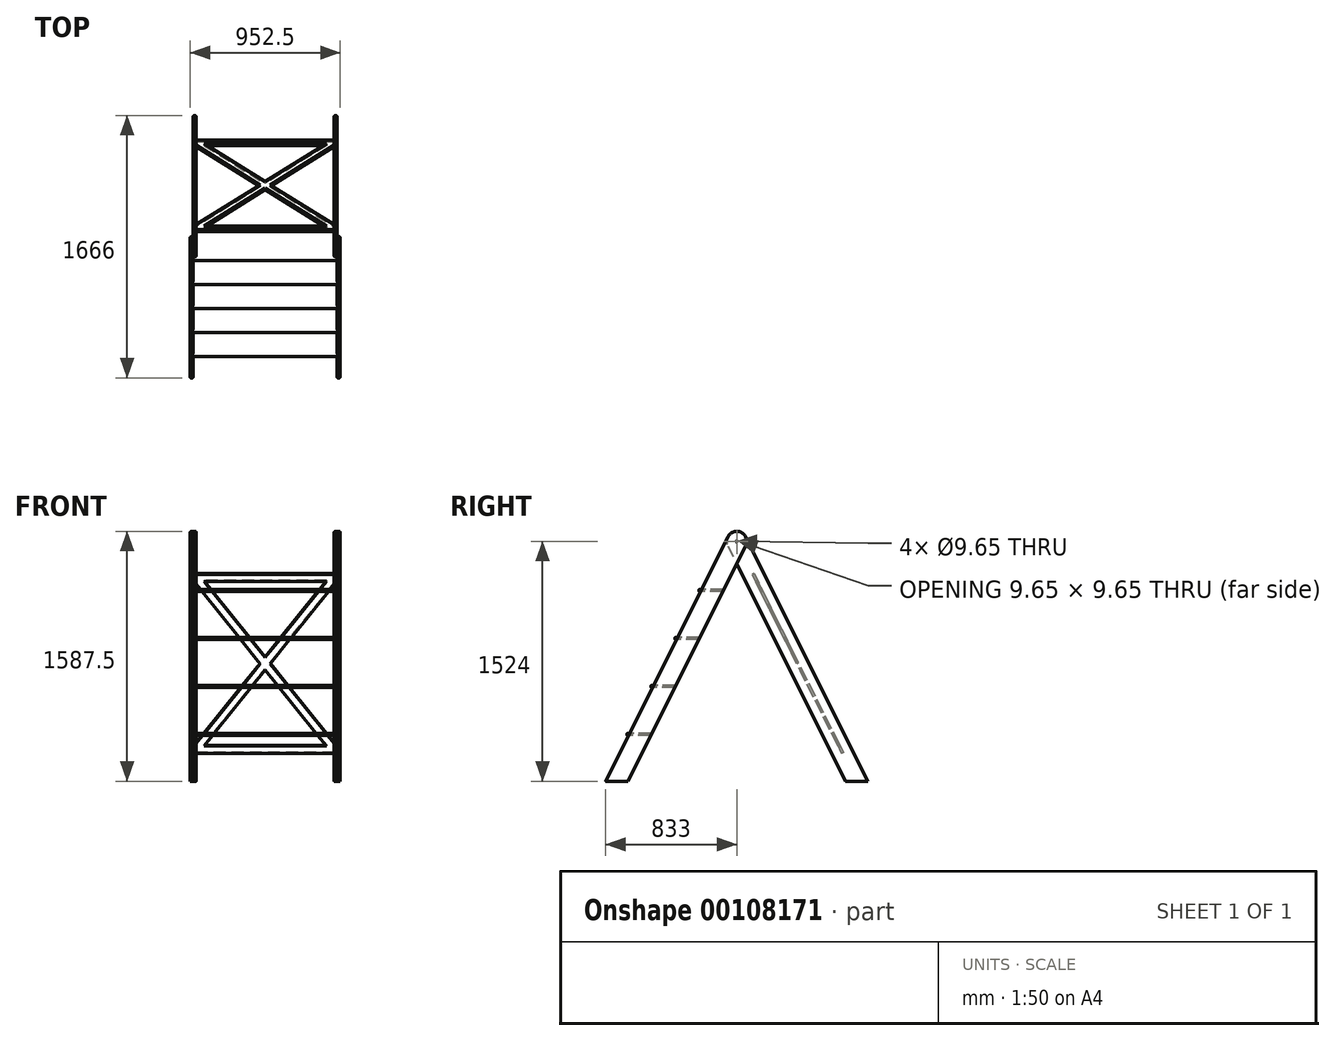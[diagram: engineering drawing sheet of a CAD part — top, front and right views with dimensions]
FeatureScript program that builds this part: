
annotation { "Feature Type Name" : "Feature", "Feature Type Description" : "" }
export const myFeature = defineFeature(function(context is Context, id is Id, definition is map)
    precondition{}
    {
        {
            var Q0;
            Q0=qCreatedBy(makeId("Right.planeOp"),FACE);
            var sketch = newSketch(context, id + "F0", { "sketchPlane" : qUnion([Q0])});
            skLineSegment(sketch, "E0", {"start": v(0, 0) * mm, "end": v(0, 1524) * mm, "construction": true});
            skLineSegment(sketch, "E1.0", {"start": v(-762, 0) * mm, "end": v(-762, 1524) * mm, "construction": true});
            skLineSegment(sketch, "E2", {"start": v(-691, 0) * mm, "end": v(-833, 0) * mm});
            skLineSegment(sketch, "E3.0", {"start": v(0, 304.8) * mm, "end": v(-1233.58, 304.8) * mm, "construction": true});
            skLineSegment(sketch, "E4.0", {"start": v(0, 609.6) * mm, "end": v(-1233.58, 609.6) * mm, "construction": true});
            skLineSegment(sketch, "E5.0", {"start": v(0, 914.4) * mm, "end": v(-1233.58, 914.4) * mm, "construction": true});
            skLineSegment(sketch, "E6.0", {"start": v(0, 1219.2) * mm, "end": v(-1233.58, 1219.2) * mm, "construction": true});
            skArc(sketch, "E7", {"start": v(-28.4, 1467.2) * mm, "mid": v(-14.59, 1462.2) * mm, "end": v(0, 1460.5) * mm, "construction": true});
            skLineSegment(sketch, "E8", {"start": v(0, 1524) * mm, "end": v(-762, 0) * mm, "construction": true});
            skLineSegment(sketch, "E9.0", {"start": v(-56.8, 1552.4) * mm, "end": v(-833, 0) * mm});
            skLineSegment(sketch, "E10.0", {"start": v(56.8, 1495.6) * mm, "end": v(-691, 0) * mm});
            skArc(sketch, "E11.trimOffspring", {"start": v(56.8, 1495.6) * mm, "mid": v(28.4, 1580.8) * mm, "end": v(-56.8, 1552.4) * mm});
            skSolve(sketch);
        }
        {
            var Q0;
            Q0 = qSketchRegion(id + "F0", true);
            extrude(context, id + "F1", {"entities" : qUnion([Q0]), "depth" : 19.05 * mm});
        }
        {
            var Q0;
            Q0=makeQuery(id+"F1.opExtrude","CAP_FACE",FACE,{"disambiguationData":[OSD([sQuery(id+"F0.wireOp",EDGE,"E2"),sQuery(id+"F0.wireOp",EDGE,"E9.0"),sQuery(id+"F0.wireOp",EDGE,"E10.0"),sQuery(id+"F0.wireOp",EDGE,"E11.trimOffspring")])],"isStart":true});
            var sketch = newSketch(context, id + "F2", { "sketchPlane" : qUnion([Q0])});
            skLineSegment(sketch, "E12.0", {"start": v(56.8, 1552.4) * mm, "end": v(229.75, 1206.5) * mm});
            skLineSegment(sketch, "E13.0", {"start": v(-56.8, 1495.6) * mm, "end": v(87.75, 1206.5) * mm});
            skLineSegment(sketch, "E14.0", {"start": v(0, 1219.2) * mm, "end": v(1233.58, 1219.2) * mm});
            skLineSegment(sketch, "E15.0", {"start": v(0, 914.4) * mm, "end": v(1233.58, 914.4) * mm});
            skLineSegment(sketch, "E16.0", {"start": v(0, 609.6) * mm, "end": v(1233.58, 609.6) * mm});
            skLineSegment(sketch, "E17.0", {"start": v(0, 304.8) * mm, "end": v(1233.58, 304.8) * mm});
            skLineSegment(sketch, "E18.0", {"start": v(0, 1206.5) * mm, "end": v(1233.58, 1206.5) * mm});
            skLineSegment(sketch, "E19.0", {"start": v(0, 901.7) * mm, "end": v(1233.58, 901.7) * mm});
            skLineSegment(sketch, "E20.0", {"start": v(0, 596.9) * mm, "end": v(1233.58, 596.9) * mm});
            skLineSegment(sketch, "E21.0", {"start": v(0, 292.1) * mm, "end": v(1233.58, 292.1) * mm});
            skLineSegment(sketch, "E22.trimOffspring", {"start": v(375.8, 914.4) * mm, "end": v(382.15, 901.7) * mm});
            skLineSegment(sketch, "E23.trimOffspring", {"start": v(233.8, 914.4) * mm, "end": v(240.15, 901.7) * mm});
            skLineSegment(sketch, "E24.trimOffspring", {"start": v(528.2, 609.6) * mm, "end": v(534.55, 596.9) * mm});
            skLineSegment(sketch, "E25.trimOffspring", {"start": v(386.2, 609.6) * mm, "end": v(392.55, 596.9) * mm});
            skLineSegment(sketch, "E26.trimOffspring", {"start": v(680.6, 304.8) * mm, "end": v(686.95, 292.1) * mm});
            skLineSegment(sketch, "E27.trimOffspring", {"start": v(538.6, 304.8) * mm, "end": v(544.95, 292.1) * mm});
            skPoint(sketch, "E28.orphan", {"position": v(833, 0) * mm});
            skPoint(sketch, "E29.orphan", {"position": v(691, 0) * mm});
            skSolve(sketch);
        }
        {
            var Q0;
            Q0 = qSketchRegion(id + "F2", true);
            extrude(context, id + "F3", {"entities" : qUnion([Q0]), "operationType" : NewBodyOperationType.REMOVE, "oppositeDirection" : true, "depth" : 6.35 * mm});
        }
        {
            var Q0;
            Q0=makeQuery(id+"F0.imprint","IMPRINT",FACE,{"disambiguationData":[TD([[makeQuery(id+"F0.imprint","IMPRINT",EDGE,{"derivedFrom":sQuery(id+"F0.wireOp",EDGE,"E2")}),-1.0]])]});
            var sketch = newSketch(context, id + "F4", { "sketchPlane" : qUnion([Q0])});
            skLineSegment(sketch, "E30.0", {"start": v(0, 1524) * mm, "end": v(-762, 0) * mm, "construction": true});
            skPoint(sketch, "E31", {"position": v(0, 1524) * mm});
            skSolve(sketch);
        }
        {
            var Q0;
            Q0=sQuery(id+"F4.wireOp",VERTEX,"E31");
            var Q1;
            Q1=makeQuery(id+"F1.opExtrude","SWEPT_BODY",BODY,{"disambiguationData":[OSD([sQuery(id+"F0.wireOp",EDGE,"E2"),sQuery(id+"F0.wireOp",EDGE,"E9.0"),sQuery(id+"F0.wireOp",EDGE,"E10.0"),sQuery(id+"F0.wireOp",EDGE,"E11.trimOffspring")])]});
            hole(context, id + "F5", {"style" : HoleStyle.SIMPLE, "endStyle" : HoleEndStyle.THROUGH, "oppositeDirection" : true, "holeDiameter" : 9.65 * mm, "locations" : qUnion([Q0]), "scope" : qUnion([Q1]), "isTappedThrough" : true});
        }
        {
            var Q0;
            {var subQ0=sQuery(id+"F0.wireOp",EDGE,"E9.0");Q0=makeQuery(id+"F3.boolean.opBoolean","SPLIT",EDGE,{"disambiguationData":[TD([makeQuery(id+"F3.opExtrude","SWEPT_FACE",FACE,{"disambiguationData":[OSD([sQuery(id+"F2.wireOp",EDGE,"E15.0")])]})])],"derivedFrom":makeQuery(id+"F1.opExtrude","CAP_EDGE",EDGE,{"disambiguationData":[OSD([subQ0])],"isStart":true})});}
            var Q1;
            Q1=makeQuery(id+"F1.opExtrude","CAP_EDGE",EDGE,{"disambiguationData":[OSD([sQuery(id+"F0.wireOp",EDGE,"E9.0")])],"isStart":false});
            var Q2;
            {var subQ0=sQuery(id+"F0.wireOp",EDGE,"E9.0");Q2=makeQuery(id+"F3.boolean.opBoolean","SPLIT",EDGE,{"disambiguationData":[TD([makeQuery(id+"F3.opExtrude","SWEPT_FACE",FACE,{"disambiguationData":[OSD([sQuery(id+"F2.wireOp",EDGE,"E16.0")])]})])],"derivedFrom":makeQuery(id+"F1.opExtrude","CAP_EDGE",EDGE,{"disambiguationData":[OSD([subQ0])],"isStart":true})});}
            var Q3;
            {var subQ0=sQuery(id+"F0.wireOp",EDGE,"E11.trimOffspring");var subQ1=sQuery(id+"F0.wireOp",EDGE,"E9.0");Q3=makeQuery(id+"F3.boolean.opBoolean","SPLIT",EDGE,{"disambiguationData":[TD([makeQuery(id+"F1.opExtrude","SWEPT_FACE",FACE,{"disambiguationData":[OSD([subQ0])]})])],"derivedFrom":makeQuery(id+"F1.opExtrude","CAP_EDGE",EDGE,{"disambiguationData":[OSD([subQ1])],"isStart":true})});}
            var Q4;
            {var subQ0=sQuery(id+"F0.wireOp",EDGE,"E10.0");Q4=makeQuery(id+"F3.boolean.opBoolean","SPLIT",EDGE,{"disambiguationData":[TD([makeQuery(id+"F3.opExtrude","SWEPT_FACE",FACE,{"disambiguationData":[OSD([sQuery(id+"F2.wireOp",EDGE,"E15.0")])]})])],"derivedFrom":makeQuery(id+"F1.opExtrude","CAP_EDGE",EDGE,{"disambiguationData":[OSD([subQ0])],"isStart":true})});}
            var Q5;
            {var subQ0=sQuery(id+"F0.wireOp",EDGE,"E10.0");Q5=makeQuery(id+"F3.boolean.opBoolean","SPLIT",EDGE,{"disambiguationData":[TD([makeQuery(id+"F3.opExtrude","SWEPT_FACE",FACE,{"disambiguationData":[OSD([sQuery(id+"F2.wireOp",EDGE,"E16.0")])]})])],"derivedFrom":makeQuery(id+"F1.opExtrude","CAP_EDGE",EDGE,{"disambiguationData":[OSD([subQ0])],"isStart":true})});}
            var Q6;
            {var subQ0=sQuery(id+"F0.wireOp",EDGE,"E10.0");Q6=makeQuery(id+"F3.boolean.opBoolean","SPLIT",EDGE,{"disambiguationData":[TD([makeQuery(id+"F3.opExtrude","SWEPT_FACE",FACE,{"disambiguationData":[OSD([sQuery(id+"F2.wireOp",EDGE,"E17.0")])]})])],"derivedFrom":makeQuery(id+"F1.opExtrude","CAP_EDGE",EDGE,{"disambiguationData":[OSD([subQ0])],"isStart":true})});}
            var Q7;
            {var subQ0=sQuery(id+"F0.wireOp",EDGE,"E9.0");Q7=makeQuery(id+"F3.boolean.opBoolean","SPLIT",EDGE,{"disambiguationData":[TD([makeQuery(id+"F3.opExtrude","SWEPT_FACE",FACE,{"disambiguationData":[OSD([sQuery(id+"F2.wireOp",EDGE,"E17.0")])]})])],"derivedFrom":makeQuery(id+"F1.opExtrude","CAP_EDGE",EDGE,{"disambiguationData":[OSD([subQ0])],"isStart":true})});}
            var Q8;
            {var subQ0=sQuery(id+"F0.wireOp",EDGE,"E2");var subQ1=sQuery(id+"F0.wireOp",EDGE,"E9.0");Q8=makeQuery(id+"F3.boolean.opBoolean","SPLIT",EDGE,{"disambiguationData":[TD([makeQuery(id+"F1.opExtrude","SWEPT_FACE",FACE,{"disambiguationData":[OSD([subQ0])]})])],"derivedFrom":makeQuery(id+"F1.opExtrude","CAP_EDGE",EDGE,{"disambiguationData":[OSD([subQ1])],"isStart":true})});}
            var Q9;
            {var subQ0=sQuery(id+"F0.wireOp",EDGE,"E2");var subQ1=sQuery(id+"F0.wireOp",EDGE,"E10.0");Q9=makeQuery(id+"F3.boolean.opBoolean","SPLIT",EDGE,{"disambiguationData":[TD([makeQuery(id+"F1.opExtrude","SWEPT_FACE",FACE,{"disambiguationData":[OSD([subQ0])]})])],"derivedFrom":makeQuery(id+"F1.opExtrude","CAP_EDGE",EDGE,{"disambiguationData":[OSD([subQ1])],"isStart":true})});}
            fillet(context, id + "F6", {"entities" : qUnion([Q0, Q1, Q2, Q3, Q4, Q5, Q6, Q7, Q8, Q9]), "radius" : 6.35 * mm, "tangentPropagation" : true, "allowEdgeOverflow" : false});
        }
        {
            var Q0;
            Q0=makeQuery(id+"F0.imprint","IMPRINT",FACE,{"disambiguationData":[TD([[makeQuery(id+"F0.imprint","IMPRINT",EDGE,{"derivedFrom":sQuery(id+"F0.wireOp",EDGE,"E2")}),-1.0]])]});
            var sketch = newSketch(context, id + "F7", { "sketchPlane" : qUnion([Q0])});
            skLineSegment(sketch, "E32.0", {"start": v(0, 0) * mm, "end": v(0, 1524) * mm});
            skLineSegment(sketch, "E33.0", {"start": v(-762, 0) * mm, "end": v(-762, 1524) * mm, "construction": true});
            skLineSegment(sketch, "E34.0", {"start": v(-56.8, 1552.4) * mm, "end": v(-833, 0) * mm, "construction": true});
            skArc(sketch, "E35.0", {"start": v(56.8, 1495.6) * mm, "mid": v(28.4, 1580.8) * mm, "end": v(-56.8, 1552.4) * mm, "construction": true});
            skLineSegment(sketch, "E36.0", {"start": v(56.8, 1495.6) * mm, "end": v(-691, 0) * mm, "construction": true});
            skLineSegment(sketch, "E37.0", {"start": v(-691, 0) * mm, "end": v(-833, 0) * mm, "construction": true});
            skArc(sketch, "E38.MirrorCS", {"start": v(-56.8, 1495.6) * mm, "mid": v(-28.4, 1580.8) * mm, "end": v(56.8, 1552.4) * mm});
            skLineSegment(sketch, "E39.MirrorCS", {"start": v(56.8, 1552.4) * mm, "end": v(833, 0) * mm});
            skLineSegment(sketch, "E40.MirrorCS", {"start": v(691, 0) * mm, "end": v(833, 0) * mm});
            skLineSegment(sketch, "E41.MirrorCS", {"start": v(-56.8, 1495.6) * mm, "end": v(691, 0) * mm});
            skCircle(sketch, "E42.0", {"center": v(0, 1524) * mm, "radius": 4.83 * mm});
            skSolve(sketch);
        }
        {
            var Q0;
            Q0 = qSketchRegion(id + "F7", true);
            extrude(context, id + "F8", {"entities" : qUnion([Q0]), "oppositeDirection" : true, "depth" : 19.05 * mm});
        }
        {
            var Q0;
            Q0=makeQuery(id+"F8.opExtrude","CAP_EDGE",EDGE,{"disambiguationData":[OSD([sQuery(id+"F7.wireOp",EDGE,"E39.MirrorCS")])],"isStart":false});
            var Q1;
            Q1=makeQuery(id+"F8.opExtrude","CAP_EDGE",EDGE,{"disambiguationData":[OSD([sQuery(id+"F7.wireOp",EDGE,"E38.MirrorCS")])],"isStart":false});
            var Q2;
            Q2=makeQuery(id+"F8.opExtrude","CAP_EDGE",EDGE,{"disambiguationData":[OSD([sQuery(id+"F7.wireOp",EDGE,"E41.MirrorCS")])],"isStart":false});
            var Q3;
            Q3=makeQuery(id+"F8.opExtrude","CAP_EDGE",EDGE,{"disambiguationData":[OSD([sQuery(id+"F7.wireOp",EDGE,"E41.MirrorCS")])],"isStart":true});
            var Q4;
            Q4=makeQuery(id+"F8.opExtrude","CAP_EDGE",EDGE,{"disambiguationData":[OSD([sQuery(id+"F7.wireOp",EDGE,"E38.MirrorCS")])],"isStart":true});
            var Q5;
            Q5=makeQuery(id+"F8.opExtrude","CAP_EDGE",EDGE,{"disambiguationData":[OSD([sQuery(id+"F7.wireOp",EDGE,"E39.MirrorCS")])],"isStart":true});
            fillet(context, id + "F9", {"entities" : qUnion([Q0, Q1, Q2, Q3, Q4, Q5]), "radius" : 6.35 * mm, "tangentPropagation" : true, "allowEdgeOverflow" : false});
        }
        {
            var Q0;
            Q0=makeQuery(id+"F8.opExtrude","SWEPT_FACE",FACE,{"disambiguationData":[OSD([sQuery(id+"F7.wireOp",EDGE,"E39.MirrorCS")])]});
            cPlane(context, id + "F10", {"entities" : qUnion([Q0]), "cplaneType" : CPlaneType.OFFSET, "offset" : 63.5 * mm, "oppositeDirection" : true, "width" : 152.4 * mm, "height" : 152.4 * mm});
        }
        {
            var Q0;
            Q0=makeQuery(id+"F0.imprint","IMPRINT",FACE,{"disambiguationData":[TD([[makeQuery(id+"F0.imprint","IMPRINT",EDGE,{"derivedFrom":sQuery(id+"F0.wireOp",EDGE,"E2")}),-1.0]])]});
            cPlane(context, id + "F11", {"entities" : qUnion([Q0]), "cplaneType" : CPlaneType.OFFSET, "offset" : 457.2 * mm, "oppositeDirection" : true, "width" : 152.4 * mm, "height" : 152.4 * mm});
        }
        {
            var Q0;
            Q0=makeQuery(id+"F1.opExtrude","SWEPT_BODY",BODY,{"disambiguationData":[OSD([sQuery(id+"F0.wireOp",EDGE,"E2"),sQuery(id+"F0.wireOp",EDGE,"E9.0"),sQuery(id+"F0.wireOp",EDGE,"E10.0"),sQuery(id+"F0.wireOp",EDGE,"E11.trimOffspring")])]});
            var Q1;
            Q1=makeQuery(id+"F8.opExtrude","SWEPT_BODY",BODY,{"disambiguationData":[OSD([sQuery(id+"F7.wireOp",EDGE,"E38.MirrorCS"),sQuery(id+"F7.wireOp",EDGE,"E39.MirrorCS"),sQuery(id+"F7.wireOp",EDGE,"E40.MirrorCS"),sQuery(id+"F7.wireOp",EDGE,"E41.MirrorCS"),sQuery(id+"F7.wireOp",EDGE,"E42.0")])]});
            var Q2;
            Q2=qCreatedBy(id+"F11.planeOp",FACE);
            mirror(context, id + "F12", {"entities" : qUnion([Q0, Q1]), "mirrorPlane" : qUnion([Q2])});
        }
        {
            var Q0;
            Q0=qCreatedBy(id+"F10.planeOp",FACE);
            var sketch = newSketch(context, id + "F13", { "sketchPlane" : qUnion([Q0])});
            skLineSegment(sketch, "E43.0", {"start": v(19.05, 1131.88) * mm, "end": v(19.05, 1062.96) * mm});
            skLineSegment(sketch, "E44.0", {"start": v(895.35, 1131.88) * mm, "end": v(895.35, 1062.96) * mm});
            skLineSegment(sketch, "E45", {"start": v(19.05, 496.88) * mm, "end": v(895.35, 496.88) * mm, "construction": true});
            skLineSegment(sketch, "E46.0", {"start": v(19.05, 1106.48) * mm, "end": v(895.35, 1106.48) * mm, "construction": true});
            skLineSegment(sketch, "E47.MirrorCS", {"start": v(19.05, -112.72) * mm, "end": v(895.35, -112.72) * mm, "construction": true});
            skLineSegment(sketch, "E48", {"start": v(895.35, -112.72) * mm, "end": v(19.05, 1106.48) * mm, "construction": true});
            skLineSegment(sketch, "E49.0", {"start": v(895.35, -69.2) * mm, "end": v(39.68, 1121.3) * mm});
            skLineSegment(sketch, "E50.MirrorCS", {"start": v(874.72, -127.55) * mm, "end": v(864.07, -112.72) * mm});
            skLineSegment(sketch, "E51.0", {"start": v(19.05, 1131.88) * mm, "end": v(895.35, 1131.88) * mm});
            skLineSegment(sketch, "E52.MirrorCS", {"start": v(19.05, 1081.08) * mm, "end": v(845.81, 1081.08) * mm});
            skLineSegment(sketch, "E53", {"start": v(457.2, 496.88) * mm, "end": v(457.2, -558.13) * mm, "construction": true});
            skLineSegment(sketch, "E54.MirrorCS", {"start": v(19.05, -87.32) * mm, "end": v(895.35, -87.32) * mm});
            skLineSegment(sketch, "E55.MirrorCS", {"start": v(19.05, -138.12) * mm, "end": v(895.35, -138.12) * mm});
            skLineSegment(sketch, "E56.MirrorCS", {"start": v(39.68, -127.55) * mm, "end": v(50.33, -112.72) * mm});
            skLineSegment(sketch, "E57.MirrorCS", {"start": v(19.05, -69.2) * mm, "end": v(845.81, 1081.08) * mm});
            skPoint(sketch, "E58.orphan", {"position": v(-1.58, -97.9) * mm});
            skPoint(sketch, "E59.orphan", {"position": v(19.05, -369.35) * mm});
            skLineSegment(sketch, "E60.trimOffspring", {"start": v(19.05, -69.2) * mm, "end": v(19.05, -138.12) * mm});
            skLineSegment(sketch, "E61.trimOffspring", {"start": v(68.59, -87.32) * mm, "end": v(915.98, 1091.65) * mm});
            skLineSegment(sketch, "E62.trimOffspring", {"start": v(845.81, -87.32) * mm, "end": v(19.05, 1062.96) * mm});
            skPoint(sketch, "E63.orphan", {"position": v(915.98, -97.9) * mm});
            skLineSegment(sketch, "E64.trimOffspring", {"start": v(895.35, -69.2) * mm, "end": v(895.35, -138.12) * mm});
            skPoint(sketch, "E65.orphan", {"position": v(895.35, -369.35) * mm});
            skLineSegment(sketch, "E66.trimOffspring", {"start": v(864.07, 1106.48) * mm, "end": v(874.72, 1121.3) * mm});
            skPoint(sketch, "E67.orphan", {"position": v(895.35, 1081.08) * mm});
            skPoint(sketch, "E68.orphan", {"position": v(19.05, 1363.1) * mm});
            skPoint(sketch, "E69.orphan", {"position": v(-1.58, 1091.65) * mm});
            skPoint(sketch, "E70.orphan", {"position": v(895.35, 1363.1) * mm});
            skSolve(sketch);
        }
        {
            var Q0;
            Q0 = qSketchRegion(id + "F13", true);
            extrude(context, id + "F14", {"entities" : qUnion([Q0]), "endBound" : BoundingType.SYMMETRIC, "depth" : 12.7 * mm});
        }
        {
            var Q0;
            Q0=makeQuery(id+"F3.boolean.opBoolean","COPY",FACE,{"derivedFrom":makeQuery(id+"F3.opExtrude","CAP_FACE",FACE,{"disambiguationData":[OSD([sQuery(id+"F2.wireOp",EDGE,"E17.0"),sQuery(id+"F2.wireOp",EDGE,"E21.0"),sQuery(id+"F2.wireOp",EDGE,"E26.trimOffspring"),sQuery(id+"F2.wireOp",EDGE,"E27.trimOffspring")])],"isStart":false})});
            var sketch = newSketch(context, id + "F15", { "sketchPlane" : qUnion([Q0])});
            skLineSegment(sketch, "E71.0", {"start": v(552.05, 292.1) * mm, "end": v(697.35, 292.1) * mm});
            skLineSegment(sketch, "E72.0", {"start": v(538.6, 304.8) * mm, "end": v(697.35, 304.8) * mm});
            skLineSegment(sketch, "E73.0", {"start": v(-56.8, 1495.6) * mm, "end": v(691, 0) * mm, "construction": true});
            skLineSegment(sketch, "E74", {"start": v(552.05, 292.1) * mm, "end": v(544.95, 292.1) * mm});
            skLineSegment(sketch, "E75", {"start": v(544.95, 292.1) * mm, "end": v(544.95, 304.8) * mm});
            skLineSegment(sketch, "E76.0", {"start": v(697.35, 292.1) * mm, "end": v(697.35, 304.8) * mm});
            skPoint(sketch, "E77.orphan", {"position": v(680.6, 304.8) * mm});
            skPoint(sketch, "E78.orphan", {"position": v(679.85, 292.1) * mm});
            skLineSegment(sketch, "E79.0", {"start": v(311.8, 596.9) * mm, "end": v(544.95, 596.9) * mm});
            skLineSegment(sketch, "E80.0", {"start": v(298.35, 609.6) * mm, "end": v(544.95, 609.6) * mm});
            skLineSegment(sketch, "E81", {"start": v(392.55, 596.9) * mm, "end": v(311.8, 596.9) * mm});
            skLineSegment(sketch, "E82", {"start": v(392.55, 596.9) * mm, "end": v(392.55, 609.6) * mm});
            skLineSegment(sketch, "E83.0", {"start": v(544.95, 596.9) * mm, "end": v(544.95, 609.6) * mm});
            skPoint(sketch, "E84.orphan", {"position": v(528.2, 609.6) * mm});
            skPoint(sketch, "E85.orphan", {"position": v(527.45, 596.9) * mm});
            skLineSegment(sketch, "E86.1", {"start": v(392.55, 596.9) * mm, "end": v(399.65, 596.9) * mm});
            skLineSegment(sketch, "E87.0", {"start": v(240.15, 901.7) * mm, "end": v(247.25, 901.7) * mm});
            skLineSegment(sketch, "E88.0", {"start": v(247.25, 901.7) * mm, "end": v(392.55, 901.7) * mm});
            skLineSegment(sketch, "E89.0", {"start": v(233.8, 914.4) * mm, "end": v(392.55, 914.4) * mm});
            skLineSegment(sketch, "E90", {"start": v(247.25, 901.7) * mm, "end": v(240.15, 901.7) * mm});
            skLineSegment(sketch, "E91", {"start": v(240.15, 901.7) * mm, "end": v(240.15, 914.4) * mm});
            skLineSegment(sketch, "E92.0", {"start": v(392.55, 901.7) * mm, "end": v(392.55, 914.4) * mm});
            skPoint(sketch, "E93.orphan", {"position": v(375.8, 914.4) * mm});
            skPoint(sketch, "E94.orphan", {"position": v(375.05, 901.7) * mm});
            skLineSegment(sketch, "E95.0", {"start": v(87.75, 1206.5) * mm, "end": v(94.85, 1206.5) * mm});
            skLineSegment(sketch, "E96.0", {"start": v(94.85, 1206.5) * mm, "end": v(240.15, 1206.5) * mm});
            skLineSegment(sketch, "E97.0", {"start": v(81.4, 1219.2) * mm, "end": v(240.15, 1219.2) * mm});
            skLineSegment(sketch, "E98", {"start": v(94.85, 1206.5) * mm, "end": v(87.75, 1206.5) * mm});
            skLineSegment(sketch, "E99", {"start": v(87.75, 1206.5) * mm, "end": v(87.75, 1219.2) * mm});
            skLineSegment(sketch, "E100.0", {"start": v(240.15, 1206.5) * mm, "end": v(240.15, 1219.2) * mm});
            skPoint(sketch, "E101.orphan", {"position": v(223.4, 1219.2) * mm});
            skPoint(sketch, "E102.orphan", {"position": v(222.65, 1206.5) * mm});
            skSolve(sketch);
        }
        {
            var Q0;
            Q0 = qSketchRegion(id + "F15", true);
            extrude(context, id + "F16", {"entities" : qUnion([Q0]), "depth" : 927.1 * mm});
        }
        {
            var Q0;
            Q0=makeQuery(id+"F16.opExtrude","CAP_EDGE",EDGE,{"disambiguationData":[OSD([sQuery(id+"F15.wireOp",EDGE,"E76.0")])],"isStart":true});
            var Q1;
            Q1=makeQuery(id+"F16.opExtrude","CAP_EDGE",EDGE,{"disambiguationData":[OSD([sQuery(id+"F15.wireOp",EDGE,"E83.0")])],"isStart":true});
            var Q2;
            Q2=makeQuery(id+"F16.opExtrude","CAP_EDGE",EDGE,{"disambiguationData":[OSD([sQuery(id+"F15.wireOp",EDGE,"E92.0")])],"isStart":true});
            var Q3;
            Q3=makeQuery(id+"F16.opExtrude","CAP_EDGE",EDGE,{"disambiguationData":[OSD([sQuery(id+"F15.wireOp",EDGE,"E100.0")])],"isStart":true});
            var Q4;
            Q4=makeQuery(id+"F16.opExtrude","CAP_EDGE",EDGE,{"disambiguationData":[OSD([sQuery(id+"F15.wireOp",EDGE,"E100.0")])],"isStart":false});
            var Q5;
            Q5=makeQuery(id+"F16.opExtrude","CAP_EDGE",EDGE,{"disambiguationData":[OSD([sQuery(id+"F15.wireOp",EDGE,"E92.0")])],"isStart":false});
            var Q6;
            Q6=makeQuery(id+"F16.opExtrude","CAP_EDGE",EDGE,{"disambiguationData":[OSD([sQuery(id+"F15.wireOp",EDGE,"E83.0")])],"isStart":false});
            var Q7;
            Q7=makeQuery(id+"F16.opExtrude","CAP_EDGE",EDGE,{"disambiguationData":[OSD([sQuery(id+"F15.wireOp",EDGE,"E76.0")])],"isStart":false});
            chamfer(context, id + "F17", {"entities" : qUnion([Q0, Q1, Q2, Q3, Q4, Q5, Q6, Q7]), "width" : 12.7 * mm, "tangentPropagation" : true});
        }
        {
            var Q0;
            Q0=makeQuery(id+"F16.opExtrude","SWEPT_EDGE",EDGE,{"disambiguationData":[OSD([sQuery(id+"F15.wireOp",EDGE,"E97.0"),sQuery(id+"F15.wireOp",EDGE,"E100.0")])]});
            var Q1;
            Q1=makeQuery(id+"F16.opExtrude","SWEPT_EDGE",EDGE,{"disambiguationData":[OSD([sQuery(id+"F15.wireOp",EDGE,"E96.0"),sQuery(id+"F15.wireOp",EDGE,"E100.0")])]});
            var Q2;
            Q2=makeQuery(id+"F16.opExtrude","SWEPT_EDGE",EDGE,{"disambiguationData":[OSD([sQuery(id+"F15.wireOp",EDGE,"E89.0"),sQuery(id+"F15.wireOp",EDGE,"E92.0")])]});
            var Q3;
            Q3=makeQuery(id+"F16.opExtrude","SWEPT_EDGE",EDGE,{"disambiguationData":[OSD([sQuery(id+"F15.wireOp",EDGE,"E88.0"),sQuery(id+"F15.wireOp",EDGE,"E92.0")])]});
            var Q4;
            Q4=makeQuery(id+"F16.opExtrude","SWEPT_EDGE",EDGE,{"disambiguationData":[OSD([sQuery(id+"F15.wireOp",EDGE,"E80.0"),sQuery(id+"F15.wireOp",EDGE,"E83.0")])]});
            var Q5;
            Q5=makeQuery(id+"F16.opExtrude","SWEPT_EDGE",EDGE,{"disambiguationData":[OSD([sQuery(id+"F15.wireOp",EDGE,"E79.0"),sQuery(id+"F15.wireOp",EDGE,"E83.0")])]});
            var Q6;
            Q6=makeQuery(id+"F16.opExtrude","SWEPT_EDGE",EDGE,{"disambiguationData":[OSD([sQuery(id+"F15.wireOp",EDGE,"E97.0"),sQuery(id+"F15.wireOp",EDGE,"E99")])]});
            var Q7;
            Q7=makeQuery(id+"F16.opExtrude","SWEPT_EDGE",EDGE,{"disambiguationData":[OSD([sQuery(id+"F15.wireOp",EDGE,"E98"),sQuery(id+"F15.wireOp",EDGE,"E99")])]});
            var Q8;
            Q8=makeQuery(id+"F16.opExtrude","SWEPT_EDGE",EDGE,{"disambiguationData":[OSD([sQuery(id+"F15.wireOp",EDGE,"E89.0"),sQuery(id+"F15.wireOp",EDGE,"E91")])]});
            var Q9;
            Q9=makeQuery(id+"F16.opExtrude","SWEPT_EDGE",EDGE,{"disambiguationData":[OSD([sQuery(id+"F15.wireOp",EDGE,"E90"),sQuery(id+"F15.wireOp",EDGE,"E91")])]});
            var Q10;
            Q10=makeQuery(id+"F16.opExtrude","SWEPT_EDGE",EDGE,{"disambiguationData":[OSD([sQuery(id+"F15.wireOp",EDGE,"E80.0"),sQuery(id+"F15.wireOp",EDGE,"E82")])]});
            var Q11;
            Q11=makeQuery(id+"F16.opExtrude","SWEPT_EDGE",EDGE,{"disambiguationData":[OSD([sQuery(id+"F15.wireOp",EDGE,"E82"),sQuery(id+"F15.wireOp",EDGE,"E86.1")])]});
            var Q12;
            Q12=makeQuery(id+"F16.opExtrude","SWEPT_EDGE",EDGE,{"disambiguationData":[OSD([sQuery(id+"F15.wireOp",EDGE,"E72.0"),sQuery(id+"F15.wireOp",EDGE,"E75")])]});
            var Q13;
            Q13=makeQuery(id+"F16.opExtrude","SWEPT_EDGE",EDGE,{"disambiguationData":[OSD([sQuery(id+"F2.wireOp",EDGE,"E27.trimOffspring"),sQuery(id+"F15.wireOp",EDGE,"E74"),sQuery(id+"F15.wireOp",EDGE,"E75")])]});
            var Q14;
            Q14=makeQuery(id+"F16.opExtrude","SWEPT_EDGE",EDGE,{"disambiguationData":[OSD([sQuery(id+"F15.wireOp",EDGE,"E72.0"),sQuery(id+"F15.wireOp",EDGE,"E76.0")])]});
            var Q15;
            Q15=makeQuery(id+"F16.opExtrude","SWEPT_EDGE",EDGE,{"disambiguationData":[OSD([sQuery(id+"F15.wireOp",EDGE,"E71.0"),sQuery(id+"F15.wireOp",EDGE,"E76.0")])]});
            fillet(context, id + "F18", {"entities" : qUnion([Q0, Q1, Q2, Q3, Q4, Q5, Q6, Q7, Q8, Q9, Q10, Q11, Q12, Q13, Q14, Q15]), "radius" : 3.17 * mm, "tangentPropagation" : true, "allowEdgeOverflow" : false});
        }
    });
